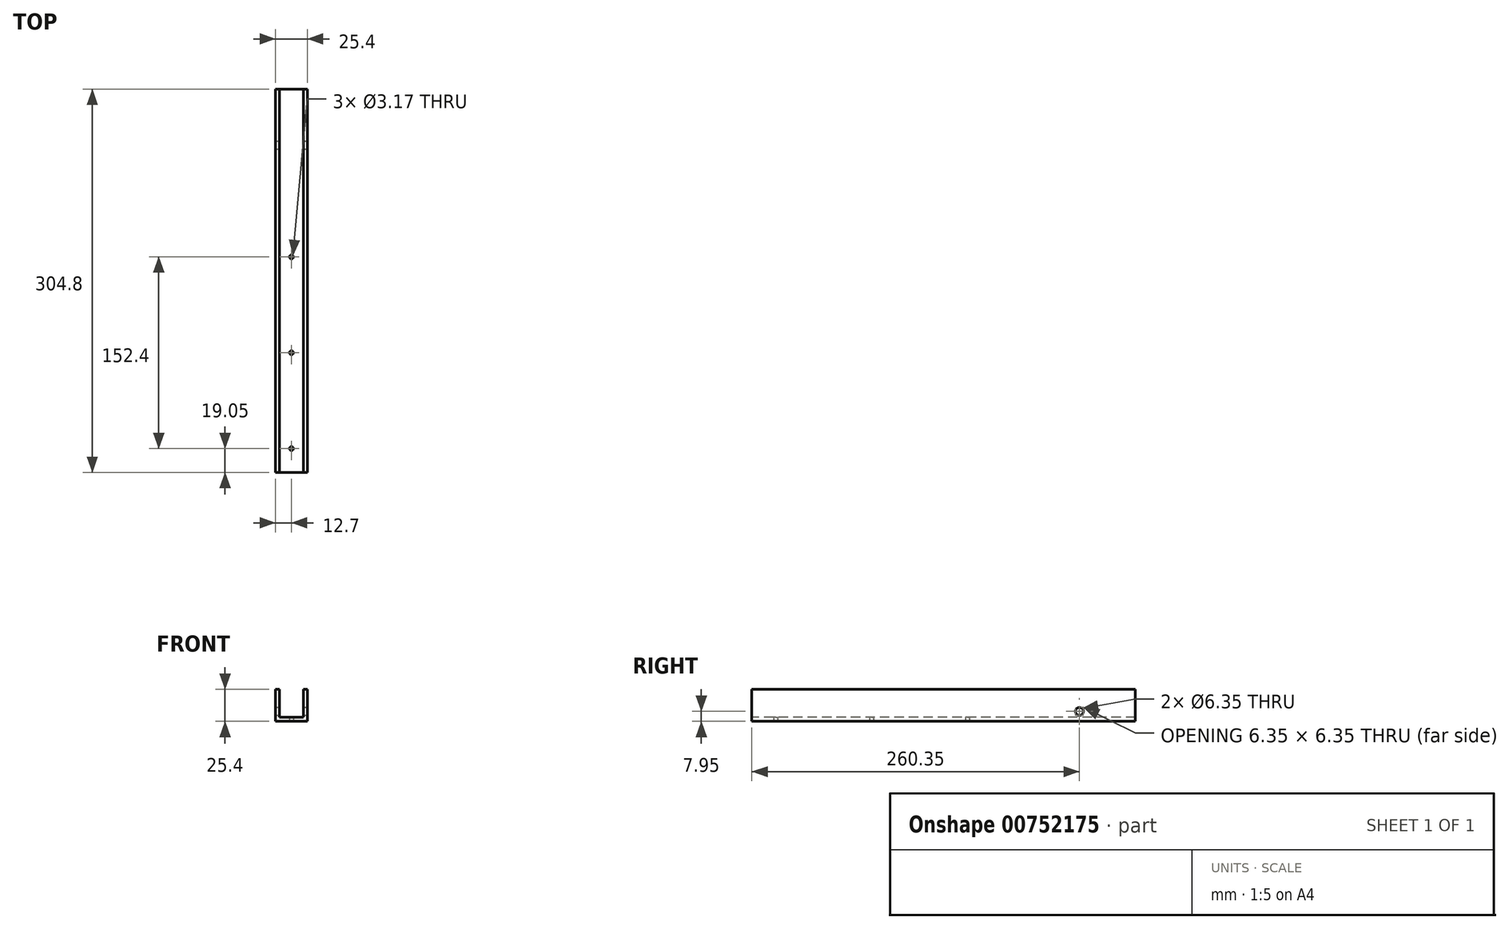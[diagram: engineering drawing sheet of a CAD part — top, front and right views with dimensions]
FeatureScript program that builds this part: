
annotation { "Feature Type Name" : "Feature", "Feature Type Description" : "" }
export const myFeature = defineFeature(function(context is Context, id is Id, definition is map)
    precondition{}
    {
        {
            var Q0;
            Q0=qCreatedBy(makeId("Front.planeOp"),FACE);
            var sketch = newSketch(context, id + "F0", { "sketchPlane" : qUnion([Q0])});
            skLineSegment(sketch, "E0", {"start": v(-12.7, 12.7) * mm, "end": v(-12.7, -12.7) * mm});
            skLineSegment(sketch, "E1", {"start": v(-12.7, -12.7) * mm, "end": v(12.7, -12.7) * mm});
            skLineSegment(sketch, "E2", {"start": v(12.7, -12.7) * mm, "end": v(12.7, 12.7) * mm});
            skLineSegment(sketch, "E3", {"start": v(12.7, 12.7) * mm, "end": v(9.53, 12.7) * mm});
            skLineSegment(sketch, "E4", {"start": v(9.53, 12.7) * mm, "end": v(9.53, -9.52) * mm});
            skLineSegment(sketch, "E5", {"start": v(9.53, -9.52) * mm, "end": v(-9.53, -9.53) * mm});
            skLineSegment(sketch, "E6", {"start": v(-9.53, -9.52) * mm, "end": v(-9.53, 12.7) * mm});
            skLineSegment(sketch, "E7", {"start": v(-9.53, 12.7) * mm, "end": v(-12.7, 12.7) * mm});
            skSolve(sketch);
        }
        {
            var Q0;
            Q0 = qSketchRegion(id + "F0", true);
            extrude(context, id + "F1", {"entities" : qUnion([Q0]), "oppositeDirection" : true, "depth" : 304.8 * mm, "offsetDistance" : 25.4 * mm});
        }
        {
            var Q0;
            Q0=makeQuery(id+"F1.opExtrude","SWEPT_FACE",FACE,{"disambiguationData":[OSD([sQuery(id+"F0.wireOp",EDGE,"E2")])]});
            var sketch = newSketch(context, id + "F2", { "sketchPlane" : qUnion([Q0])});
            skCircle(sketch, "E8", {"center": v(260.35, -4.75) * mm, "radius": 3.18 * mm});
            skSolve(sketch);
        }
        {
            var Q0;
            Q0 = qSketchRegion(id + "F2", true);
            var Q1;
            Q1=makeQuery(id+"F1.opExtrude","SWEPT_FACE",FACE,{"disambiguationData":[OSD([sQuery(id+"F0.wireOp",EDGE,"E0")])]});
            extrude(context, id + "F3", {"entities" : qUnion([Q0]), "operationType" : NewBodyOperationType.REMOVE, "endBound" : BoundingType.UP_TO_SURFACE, "oppositeDirection" : true, "depth" : 25.4 * mm, "endBoundEntityFace" : qUnion([Q1]), "offsetDistance" : 25.4 * mm});
        }
        {
            var Q0;
            Q0=makeQuery(id+"F1.opExtrude","SWEPT_FACE",FACE,{"disambiguationData":[OSD([sQuery(id+"F0.wireOp",EDGE,"E1")])]});
            var sketch = newSketch(context, id + "F4", { "sketchPlane" : qUnion([Q0])});
            skLineSegment(sketch, "E9", {"start": v(0, 10.52) * mm, "end": v(0, -214.45) * mm, "construction": true});
            skPoint(sketch, "E9.startSnap0", {"position": v(0, 0) * mm});
            skLineSegment(sketch, "E10", {"start": v(19.06, -19.05) * mm, "end": v(0, -19.05) * mm, "construction": true});
            skLineSegment(sketch, "E11", {"start": v(21.85, -95.25) * mm, "end": v(0, -95.25) * mm, "construction": true});
            skLineSegment(sketch, "E12", {"start": v(23, -171.45) * mm, "end": v(0, -171.45) * mm, "construction": true});
            skCircle(sketch, "E13", {"center": v(0, -19.05) * mm, "radius": 1.59 * mm});
            skCircle(sketch, "E14", {"center": v(0, -95.25) * mm, "radius": 1.59 * mm});
            skCircle(sketch, "E15", {"center": v(0, -171.45) * mm, "radius": 1.59 * mm});
            skSolve(sketch);
        }
        {
            var Q0;
            Q0 = qSketchRegion(id + "F4", true);
            extrude(context, id + "F5", {"entities" : qUnion([Q0]), "operationType" : NewBodyOperationType.REMOVE, "oppositeDirection" : true, "depth" : 25.4 * mm, "offsetDistance" : 25.4 * mm});
        }
    });
